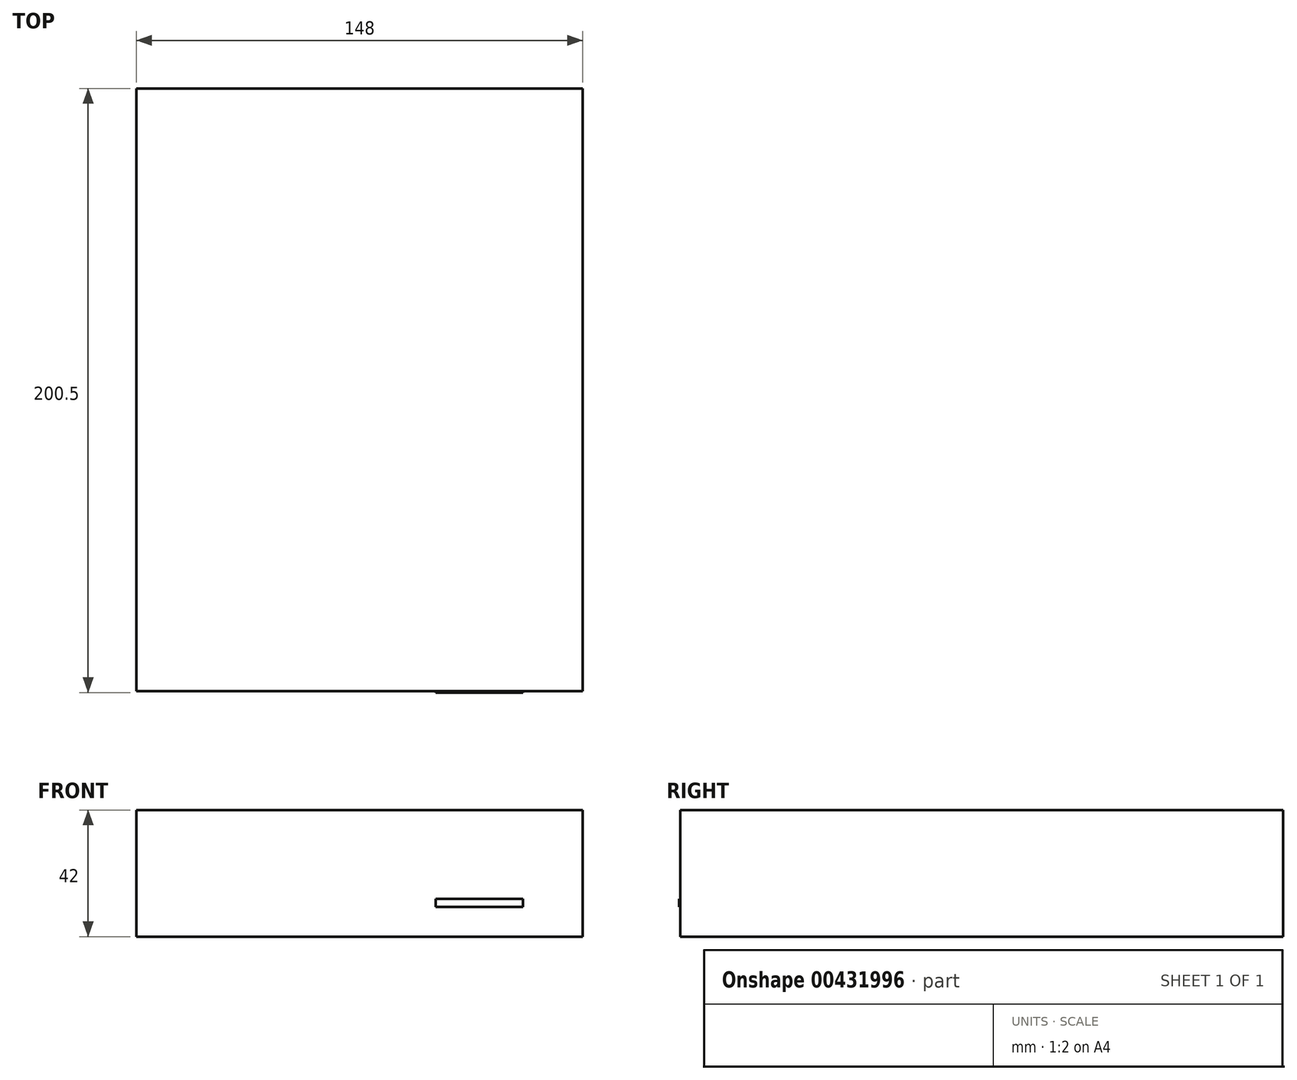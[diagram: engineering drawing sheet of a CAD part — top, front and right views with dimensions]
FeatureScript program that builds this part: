
annotation { "Feature Type Name" : "Feature", "Feature Type Description" : "" }
export const myFeature = defineFeature(function(context is Context, id is Id, definition is map)
    precondition{}
    {
        {
            var Q0;
            Q0=qCreatedBy(makeId("Top.planeOp"),FACE);
            var sketch = newSketch(context, id + "F0", { "sketchPlane" : qUnion([Q0])});
            skLineSegment(sketch, "E0.bottom", {"start": v(-74, 100) * mm, "end": v(74, 100) * mm});
            skLineSegment(sketch, "E0.top", {"start": v(-74, -100) * mm, "end": v(74, -100) * mm});
            skLineSegment(sketch, "E0.left", {"start": v(-74, 100) * mm, "end": v(-74, -100) * mm});
            skLineSegment(sketch, "E0.right", {"start": v(74, 100) * mm, "end": v(74, -100) * mm});
            skPoint(sketch, "E0.middle", {"position": v(0, 0) * mm});
            skSolve(sketch);
        }
        {
            var Q0;
            Q0=qSketchRegion(id+"F0",true);
            extrude(context, id + "F1", {"entities" : qUnion([Q0]), "depth" : 42 * mm});
        }
        {
            var Q0;
            Q0=makeQuery(id+"F1.opExtrude","SWEPT_FACE",FACE,{"disambiguationData":[OSD([sQuery(id+"F0.wireOp",EDGE,"E0.top")])]});
            var sketch = newSketch(context, id + "F2", { "sketchPlane" : qUnion([Q0])});
            skLineSegment(sketch, "E1.bottom", {"start": v(54.26, 9.86) * mm, "end": v(25.3, 9.86) * mm});
            skLineSegment(sketch, "E1.top", {"start": v(54.26, 12.57) * mm, "end": v(25.3, 12.57) * mm});
            skLineSegment(sketch, "E1.left", {"start": v(54.26, 9.86) * mm, "end": v(54.26, 12.57) * mm});
            skLineSegment(sketch, "E1.right", {"start": v(25.3, 9.86) * mm, "end": v(25.3, 12.57) * mm});
            skPoint(sketch, "E1.middle", {"position": v(39.78, 11.21) * mm});
            skSolve(sketch);
        }
        {
            var Q0;
            Q0=qSketchRegion(id+"F2",true);
            extrude(context, id + "F3", {"entities" : qUnion([Q0]), "operationType" : NewBodyOperationType.ADD, "depth" : 0.5 * mm});
        }
    });
